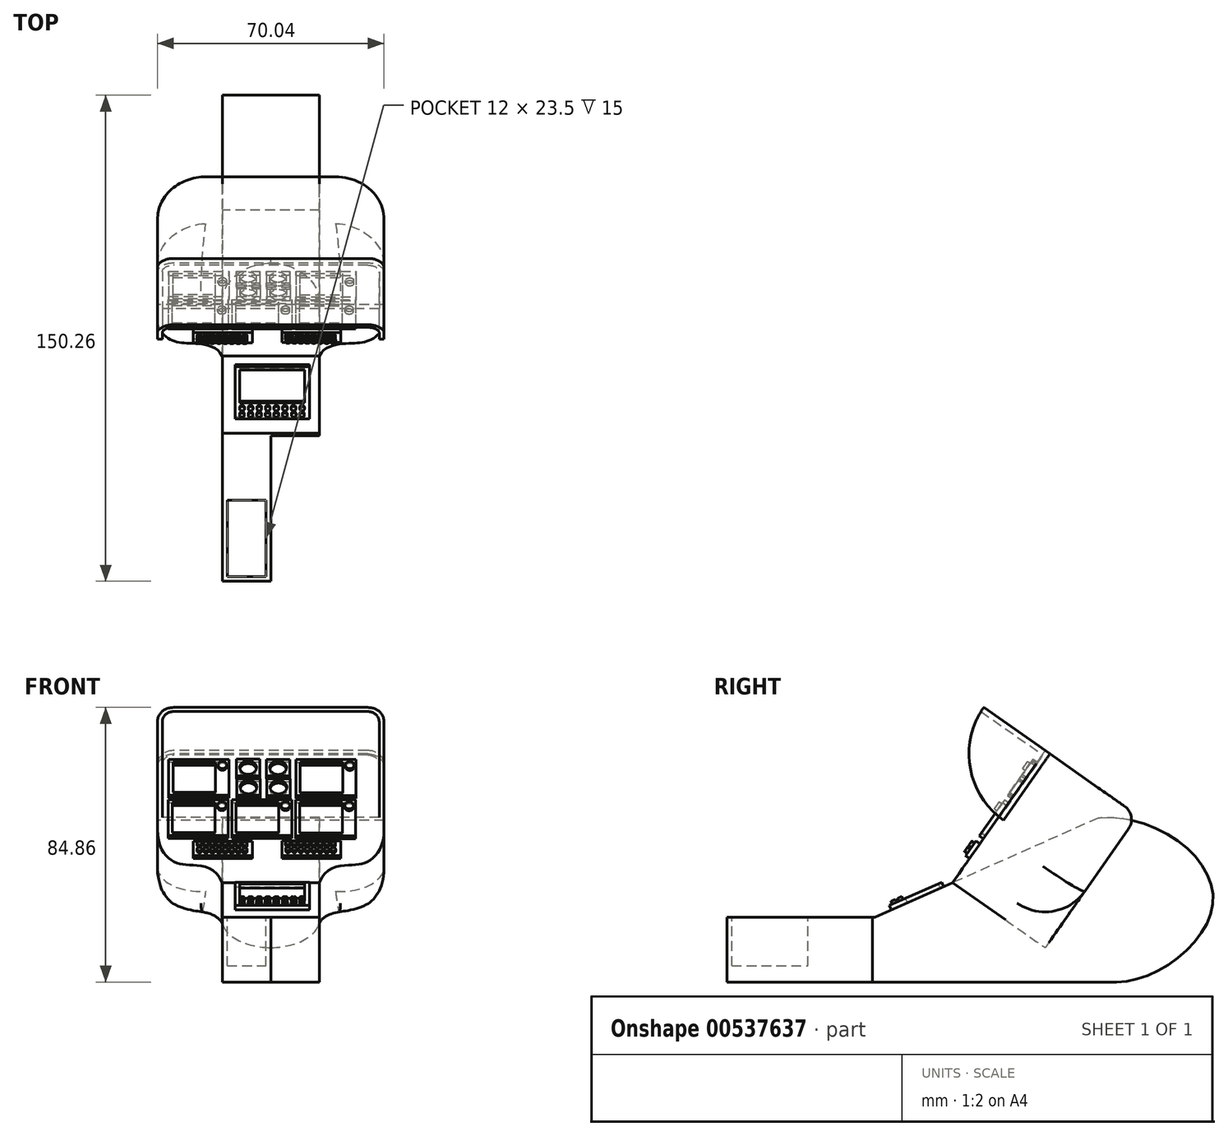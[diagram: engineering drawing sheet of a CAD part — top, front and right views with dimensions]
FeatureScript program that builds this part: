
annotation { "Feature Type Name" : "Feature", "Feature Type Description" : "" }
export const myFeature = defineFeature(function(context is Context, id is Id, definition is map)
    precondition{}
    {
        {
            var Q0;
            Q0=qCreatedBy(makeId("Right.planeOp"),FACE);
            var sketch = newSketch(context, id + "F0", { "sketchPlane" : qUnion([Q0])});
            skLineSegment(sketch, "E0", {"start": v(-60.7, 0) * mm, "end": v(59.7, 0) * mm});
            skLineSegment(sketch, "E1", {"start": v(-60.7, 0) * mm, "end": v(-60.7, 20) * mm});
            skLineSegment(sketch, "E2", {"start": v(-60.7, 20) * mm, "end": v(30.7, 20) * mm});
            skLineSegment(sketch, "E3", {"start": v(30.7, 20) * mm, "end": v(54, 50.65) * mm});
            skFitSpline(sketch, "E4", {"points": [v(59.7, 0) * mm, v(89.55, 25.37) * mm, v(54, 50.65) * mm], "startDerivative": vector(77.96, 0) * mm, "endDerivative": vector(-105.4, -8.94) * mm});
            skPoint(sketch, "E5.start.orphan", {"position": v(56.86, 25.33) * mm});
            skLineSegment(sketch, "E6", {"start": v(54, 50.65) * mm, "end": v(-15, 20) * mm});
            skSolve(sketch);
        }
        {
            var Q0;
            Q0 = qSketchRegion(id + "F0", true);
            extrude(context, id + "F1", {"entities" : qUnion([Q0]), "depth" : 30 * mm, "offsetDistance" : 25 * mm});
        }
        {
            var Q0;
            Q0=makeQuery(id+"F1.opExtrude","SWEPT_FACE",FACE,{"disambiguationData":[OSD([sQuery(id+"F0.wireOp",EDGE,"E2")])]});
            var sketch = newSketch(context, id + "F2", { "sketchPlane" : qUnion([Q0])});
            skLineSegment(sketch, "E7.bottom", {"start": v(30, -60.7) * mm, "end": v(15, -60.7) * mm});
            skLineSegment(sketch, "E7.top", {"start": v(30, -15.7) * mm, "end": v(15, -15.7) * mm});
            skLineSegment(sketch, "E7.left", {"start": v(30, -60.7) * mm, "end": v(30, -15.7) * mm});
            skLineSegment(sketch, "E7.right", {"start": v(15, -60.7) * mm, "end": v(15, -15.7) * mm});
            skSolve(sketch);
        }
        {
            var Q0;
            Q0=makeQuery(id+"F2.imprint","IMPRINT",FACE,{"disambiguationData":[TD([[makeQuery(id+"F2.imprint","IMPRINT",EDGE,{"derivedFrom":sQuery(id+"F2.wireOp",EDGE,"E7.bottom")}),-1.0]])]});
            extrude(context, id + "F3", {"entities" : qUnion([Q0]), "operationType" : NewBodyOperationType.REMOVE, "oppositeDirection" : true, "depth" : 25 * mm, "offsetDistance" : 25 * mm});
        }
        {
            var Q0;
            Q0=qCreatedBy(makeId("Front.planeOp"),FACE);
            var sketch = newSketch(context, id + "F4", { "sketchPlane" : qUnion([Q0])});
            skLineSegment(sketch, "E8.bottom", {"start": v(-58.83, 0) * mm, "end": v(-73.91, 0) * mm});
            skLineSegment(sketch, "E8.top", {"start": v(-58.83, 49.9) * mm, "end": v(-93.85, 49.9) * mm});
            skLineSegment(sketch, "E8.left", {"start": v(-58.83, 0) * mm, "end": v(-58.83, 49.9) * mm});
            skLineSegment(sketch, "E8.right", {"start": v(-93.85, 20.22) * mm, "end": v(-93.85, 49.9) * mm});
            skFitSpline(sketch, "E9", {"points": [v(-93.85, 20.22) * mm, v(-88.82, 8.01) * mm, v(-83.08, 6.66) * mm, v(-73.91, 0) * mm], "startDerivative": vector(0, -55.1) * mm, "endDerivative": vector(14.58, -51.04) * mm});
            skLineSegment(sketch, "E10.MirrorCS", {"start": v(-58.83, 0) * mm, "end": v(-43.76, 0) * mm});
            skLineSegment(sketch, "E11.MirrorCS", {"start": v(-23.81, 20.22) * mm, "end": v(-23.81, 49.9) * mm});
            skLineSegment(sketch, "E12.MirrorCS", {"start": v(-58.83, 49.9) * mm, "end": v(-23.81, 49.9) * mm});
            skFitSpline(sketch, "E13.MirrorCS", {"points": [v(-23.81, 20.22) * mm, v(-28.84, 8.01) * mm, v(-34.59, 6.66) * mm, v(-43.76, 0) * mm], "startDerivative": vector(0, -55.1) * mm, "endDerivative": vector(-14.58, -51.04) * mm});
            skSolve(sketch);
        }
        {
            var Q0;
            Q0 = qSketchRegion(id + "F4", true);
            extrude(context, id + "F5", {"entities" : qUnion([Q0]), "oppositeDirection" : true, "depth" : 35 * mm, "offsetDistance" : 25 * mm});
        }
        {
            var Q0;
            Q0=makeQuery(id+"F5.opExtrude","CAP_EDGE",EDGE,{"disambiguationData":[OSD([sQuery(id+"F4.wireOp",EDGE,"E13.MirrorCS")])],"isStart":false});
            var Q1;
            Q1=makeQuery(id+"F5.opExtrude","CAP_EDGE",EDGE,{"disambiguationData":[OSD([sQuery(id+"F4.wireOp",EDGE,"E11.MirrorCS")])],"isStart":false});
            var Q2;
            Q2=makeQuery(id+"F5.opExtrude","CAP_EDGE",EDGE,{"disambiguationData":[OSD([sQuery(id+"F4.wireOp",EDGE,"E8.right")])],"isStart":false});
            var Q3;
            Q3=makeQuery(id+"F5.opExtrude","CAP_EDGE",EDGE,{"disambiguationData":[OSD([sQuery(id+"F4.wireOp",EDGE,"E9")])],"isStart":false});
            fillet(context, id + "F6", {"entities" : qUnion([Q0, Q1, Q2, Q3]), "radius" : 15 * mm, "tangentPropagation" : true, "allowEdgeOverflow" : false});
        }
        {
            var Q0;
            Q0=makeQuery(id+"F6.opFillet","BLEND_EDGE",EDGE,{"blendedFrom":[makeQuery(id+"F5.opExtrude","CAP_EDGE",EDGE,{"disambiguationData":[OSD([sQuery(id+"F4.wireOp",EDGE,"E11.MirrorCS")])],"isStart":false}),makeQuery(id+"F5.opExtrude","SWEPT_FACE",FACE,{"disambiguationData":[OSD([sQuery(id+"F4.wireOp",EDGE,"E8.top"),sQuery(id+"F4.wireOp",EDGE,"E12.MirrorCS")])]})],"blendedInto":[makeQuery(id+"F5.opExtrude","SWEPT_FACE",FACE,{"disambiguationData":[OSD([sQuery(id+"F4.wireOp",EDGE,"E8.top"),sQuery(id+"F4.wireOp",EDGE,"E12.MirrorCS")])]})]});
            var Q1;
            Q1=makeQuery(id+"F5.opExtrude","CAP_EDGE",EDGE,{"disambiguationData":[OSD([sQuery(id+"F4.wireOp",EDGE,"E8.top"),sQuery(id+"F4.wireOp",EDGE,"E12.MirrorCS")])],"isStart":false});
            var Q2;
            Q2=makeQuery(id+"F6.opFillet","BLEND_EDGE",EDGE,{"blendedFrom":[makeQuery(id+"F5.opExtrude","CAP_EDGE",EDGE,{"disambiguationData":[OSD([sQuery(id+"F4.wireOp",EDGE,"E8.right")])],"isStart":false}),makeQuery(id+"F5.opExtrude","SWEPT_FACE",FACE,{"disambiguationData":[OSD([sQuery(id+"F4.wireOp",EDGE,"E8.top"),sQuery(id+"F4.wireOp",EDGE,"E12.MirrorCS")])]})],"blendedInto":[makeQuery(id+"F5.opExtrude","SWEPT_FACE",FACE,{"disambiguationData":[OSD([sQuery(id+"F4.wireOp",EDGE,"E8.top"),sQuery(id+"F4.wireOp",EDGE,"E12.MirrorCS")])]})]});
            fillet(context, id + "F7", {"entities" : qUnion([Q0, Q1, Q2]), "radius" : 5 * mm, "tangentPropagation" : true, "allowEdgeOverflow" : false});
        }
        {
            var Q0;
            Q0=makeQuery(id+"F5.opExtrude","SWEPT_FACE",FACE,{"disambiguationData":[OSD([sQuery(id+"F4.wireOp",EDGE,"E8.right")])]});
            var sketch = newSketch(context, id + "F8", { "sketchPlane" : qUnion([Q0])});
            skPoint(sketch, "E14.0", {"position": v(0, 49.9) * mm});
            skLineSegment(sketch, "E15", {"start": v(0, 49.9) * mm, "end": v(0, 24.9) * mm});
            skArc(sketch, "E16", {"start": v(0, 24.9) * mm, "mid": v(17.68, 32.23) * mm, "end": v(25, 49.9) * mm});
            skLineSegment(sketch, "E17", {"start": v(25, 49.9) * mm, "end": v(0, 49.9) * mm});
            skSolve(sketch);
        }
        {
            var Q0;
            {var subQ4=sQuery(id+"F8.wireOp",EDGE,"E16");Q0=makeQuery(id+"F8.imprint","IMPRINT",FACE,{"disambiguationData":[TD([[makeQuery(id+"F8.imprint","IMPRINT",EDGE,{"derivedFrom":subQ4}),1.0]])]});}
            var Q1;
            Q1=makeQuery(id+"F5.opExtrude","SWEPT_FACE",FACE,{"disambiguationData":[OSD([sQuery(id+"F4.wireOp",EDGE,"E11.MirrorCS")])]});
            extrude(context, id + "F9", {"entities" : qUnion([Q0]), "endBound" : BoundingType.UP_TO_SURFACE, "oppositeDirection" : true, "depth" : 25 * mm, "endBoundEntityFace" : qUnion([Q1]), "offsetDistance" : 25 * mm});
        }
        {
            var Q0;
            Q0=makeQuery(id+"F9.opExtrude","CAP_EDGE",EDGE,{"disambiguationData":[OSD([sQuery(id+"F8.wireOp",EDGE,"E17")])],"isStart":true});
            var Q1;
            Q1=makeQuery(id+"F9.opExtrude","CAP_EDGE",EDGE,{"disambiguationData":[OSD([sQuery(id+"F8.wireOp",EDGE,"E17")])],"isStart":false});
            fillet(context, id + "F10", {"entities" : qUnion([Q0, Q1]), "radius" : 5 * mm, "tangentPropagation" : true, "allowEdgeOverflow" : false});
        }
        {
            var Q0;
            Q0=makeQuery(id+"F9.opExtrude","SWEPT_FACE",FACE,{"disambiguationData":[OSD([sQuery(id+"F8.wireOp",EDGE,"E16")])]});
            shell(context, id + "F11", {"entities" : qUnion([Q0]), "thickness" : 1.5 * mm});
        }
        {
            var Q0;
            Q0=makeQuery(id+"F5.opExtrude","SWEPT_BODY",BODY,{"disambiguationData":[OSD([sQuery(id+"F4.wireOp",EDGE,"E8.top"),sQuery(id+"F4.wireOp",EDGE,"E8.right"),sQuery(id+"F4.wireOp",EDGE,"E8.bottom"),sQuery(id+"F4.wireOp",EDGE,"E9"),sQuery(id+"F4.wireOp",EDGE,"E11.MirrorCS"),sQuery(id+"F4.wireOp",EDGE,"E10.MirrorCS"),sQuery(id+"F4.wireOp",EDGE,"E12.MirrorCS"),sQuery(id+"F4.wireOp",EDGE,"E13.MirrorCS")])]});
            var Q1;
            Q1=makeQuery(id+"F9.opExtrude","SWEPT_BODY",BODY,{"disambiguationData":[OSD([sQuery(id+"F8.wireOp",EDGE,"E15"),sQuery(id+"F8.wireOp",EDGE,"E16"),sQuery(id+"F8.wireOp",EDGE,"E17")])]});
            var Q2;
            Q2=makeQuery(id+"F5.opExtrude","CAP_EDGE",EDGE,{"disambiguationData":[OSD([sQuery(id+"F4.wireOp",EDGE,"E8.bottom"),sQuery(id+"F4.wireOp",EDGE,"E10.MirrorCS")])],"isStart":true});
            transform(context, id + "F12", {"entities" : qUnion([Q0, Q1]), "transformType" : TransformType.ROTATION, "transformAxis" : qUnion([Q2]), "angle" : 35 * degree, "makeCopy" : false});
        }
        {
            var Q0;
            Q0=makeQuery(id+"F1.opExtrude","CAP_FACE",FACE,{"disambiguationData":[OSD([sQuery(id+"F0.wireOp",EDGE,"E0"),sQuery(id+"F0.wireOp",EDGE,"E1"),sQuery(id+"F0.wireOp",EDGE,"E2"),sQuery(id+"F0.wireOp",EDGE,"E4"),sQuery(id+"F0.wireOp",EDGE,"E6")])],"isStart":false});
            var sketch = newSketch(context, id + "F13", { "sketchPlane" : qUnion([Q0])});
            skPoint(sketch, "E18.0", {"position": v(-60.7, 0) * mm});
            skPoint(sketch, "E19", {"position": v(9, 30.67) * mm});
            skSolve(sketch);
        }
        {
            var Q0;
            Q0=makeQuery(id+"F9.opExtrude","SWEPT_BODY",BODY,{"disambiguationData":[OSD([sQuery(id+"F8.wireOp",EDGE,"E15"),sQuery(id+"F8.wireOp",EDGE,"E16"),sQuery(id+"F8.wireOp",EDGE,"E17")])]});
            var Q1;
            Q1=makeQuery(id+"F5.opExtrude","SWEPT_BODY",BODY,{"disambiguationData":[OSD([sQuery(id+"F4.wireOp",EDGE,"E8.top"),sQuery(id+"F4.wireOp",EDGE,"E8.right"),sQuery(id+"F4.wireOp",EDGE,"E8.bottom"),sQuery(id+"F4.wireOp",EDGE,"E9"),sQuery(id+"F4.wireOp",EDGE,"E11.MirrorCS"),sQuery(id+"F4.wireOp",EDGE,"E10.MirrorCS"),sQuery(id+"F4.wireOp",EDGE,"E12.MirrorCS"),sQuery(id+"F4.wireOp",EDGE,"E13.MirrorCS")])]});
            var Q2;
            Q2=makeQuery(id+"F5.opExtrude","CAP_VERTEX",VERTEX,{"disambiguationData":[OSD([sQuery(id+"F4.wireOp",EDGE,"E10.MirrorCS"),sQuery(id+"F4.wireOp",EDGE,"E13.MirrorCS")])],"isStart":true});
            var Q3;
            Q3=sQuery(id+"F13.wireOp",VERTEX,"E19");
            transform(context, id + "F14", {"entities" : qUnion([Q0, Q1]), "transformType" : TransformType.TRANSLATION_ENTITY, "oppositeDirectionEntity" : false, "transformLine" : qUnion([Q2, Q3]), "makeCopy" : false});
        }
        {
            var Q0;
            Q0=makeQuery(id+"F9.opExtrude","CAP_FACE",FACE,{"disambiguationData":[OSD([sQuery(id+"F8.wireOp",EDGE,"E15"),sQuery(id+"F8.wireOp",EDGE,"E16"),sQuery(id+"F8.wireOp",EDGE,"E17")])],"isStart":false});
            var sketch = newSketch(context, id + "F15", { "sketchPlane" : qUnion([Q0])});
            skLineSegment(sketch, "E20", {"start": v(29.02, 59.26) * mm, "end": v(30.5, 58.23) * mm});
            skSolve(sketch);
        }
        {
            var Q0;
            Q0=makeQuery(id+"F9.opExtrude","SWEPT_BODY",BODY,{"disambiguationData":[OSD([sQuery(id+"F8.wireOp",EDGE,"E15"),sQuery(id+"F8.wireOp",EDGE,"E16"),sQuery(id+"F8.wireOp",EDGE,"E17")])]});
            var Q1;
            Q1=sQuery(id+"F15.wireOp",VERTEX,"E20.start");
            var Q2;
            Q2=sQuery(id+"F15.wireOp",VERTEX,"E20.end");
            transform(context, id + "F16", {"entities" : qUnion([Q0]), "transformType" : TransformType.TRANSLATION_ENTITY, "oppositeDirectionEntity" : false, "transformLine" : qUnion([Q1, Q2]), "makeCopy" : false});
        }
        {
            var Q0;
            Q0=makeQuery(id+"F1.opExtrude","SWEPT_FACE",FACE,{"disambiguationData":[OSD([sQuery(id+"F0.wireOp",EDGE,"E2")])]});
            var sketch = newSketch(context, id + "F17", { "sketchPlane" : qUnion([Q0])});
            skLineSegment(sketch, "E21", {"start": v(0, -60.7) * mm, "end": v(1.5, -60.7) * mm});
            skLineSegment(sketch, "E22", {"start": v(1.5, -60.7) * mm, "end": v(1.5, -59.2) * mm});
            skLineSegment(sketch, "E23.bottom", {"start": v(1.5, -59.2) * mm, "end": v(13.5, -59.2) * mm});
            skLineSegment(sketch, "E23.top", {"start": v(1.5, -35.7) * mm, "end": v(13.5, -35.7) * mm});
            skLineSegment(sketch, "E23.left", {"start": v(1.5, -59.2) * mm, "end": v(1.5, -35.7) * mm});
            skLineSegment(sketch, "E23.right", {"start": v(13.5, -59.2) * mm, "end": v(13.5, -35.7) * mm});
            skSolve(sketch);
        }
        {
            var Q0;
            Q0=makeQuery(id+"F17.imprint","IMPRINT",FACE,{"disambiguationData":[TD([[makeQuery(id+"F17.imprint","IMPRINT",EDGE,{"derivedFrom":sQuery(id+"F17.wireOp",EDGE,"E23.bottom")}),1.0]])]});
            extrude(context, id + "F18", {"entities" : qUnion([Q0]), "operationType" : NewBodyOperationType.REMOVE, "oppositeDirection" : true, "depth" : 15 * mm, "offsetDistance" : 25 * mm});
        }
        {
            var Q0;
            Q0=makeQuery(id+"F5.opExtrude","CAP_FACE",FACE,{"disambiguationData":[OSD([sQuery(id+"F4.wireOp",EDGE,"E8.top"),sQuery(id+"F4.wireOp",EDGE,"E8.right"),sQuery(id+"F4.wireOp",EDGE,"E8.bottom"),sQuery(id+"F4.wireOp",EDGE,"E9"),sQuery(id+"F4.wireOp",EDGE,"E11.MirrorCS"),sQuery(id+"F4.wireOp",EDGE,"E10.MirrorCS"),sQuery(id+"F4.wireOp",EDGE,"E12.MirrorCS"),sQuery(id+"F4.wireOp",EDGE,"E13.MirrorCS")])],"isStart":true});
            var sketch = newSketch(context, id + "F19", { "sketchPlane" : qUnion([Q0])});
            skLineSegment(sketch, "E24.bottom", {"start": v(-16.58, 75.82) * mm, "end": v(1.98, 75.82) * mm});
            skLineSegment(sketch, "E24.top", {"start": v(-16.58, 62.23) * mm, "end": v(1.98, 62.23) * mm});
            skLineSegment(sketch, "E24.left", {"start": v(-16.58, 75.82) * mm, "end": v(-16.58, 62.23) * mm});
            skLineSegment(sketch, "E24.right", {"start": v(1.98, 75.82) * mm, "end": v(1.98, 62.23) * mm});
            skPoint(sketch, "E25.oppositeSnap0", {"position": v(-20.1, 62.85) * mm});
            skLineSegment(sketch, "E26.bottom", {"start": v(-15.3, 63.3) * mm, "end": v(-2.13, 63.3) * mm});
            skLineSegment(sketch, "E26.top", {"start": v(-15.3, 74.71) * mm, "end": v(-2.13, 74.71) * mm});
            skLineSegment(sketch, "E26.left", {"start": v(-15.3, 63.3) * mm, "end": v(-15.3, 74.71) * mm});
            skLineSegment(sketch, "E26.right", {"start": v(-2.13, 63.3) * mm, "end": v(-2.13, 74.71) * mm});
            skCircle(sketch, "E27", {"center": v(0, 73.02) * mm, "radius": 1.34 * mm});
            skLineSegment(sketch, "E28.bottom", {"start": v(22.78, 75.76) * mm, "end": v(41.33, 75.76) * mm});
            skLineSegment(sketch, "E28.top", {"start": v(22.78, 62.16) * mm, "end": v(41.33, 62.16) * mm});
            skLineSegment(sketch, "E28.left", {"start": v(22.78, 75.76) * mm, "end": v(22.78, 62.16) * mm});
            skLineSegment(sketch, "E28.right", {"start": v(41.33, 75.76) * mm, "end": v(41.33, 62.16) * mm});
            skLineSegment(sketch, "E29.bottom", {"start": v(24.05, 63.25) * mm, "end": v(37.23, 63.25) * mm});
            skLineSegment(sketch, "E29.top", {"start": v(24.05, 74.65) * mm, "end": v(37.23, 74.65) * mm});
            skLineSegment(sketch, "E29.left", {"start": v(24.05, 63.25) * mm, "end": v(24.05, 74.65) * mm});
            skLineSegment(sketch, "E29.right", {"start": v(37.23, 63.25) * mm, "end": v(37.23, 74.65) * mm});
            skCircle(sketch, "E30", {"center": v(39.36, 72.96) * mm, "radius": 1.34 * mm});
            skLineSegment(sketch, "E31.bottom", {"start": v(-16.76, 60.6) * mm, "end": v(1.8, 60.6) * mm});
            skLineSegment(sketch, "E31.top", {"start": v(-16.76, 47.01) * mm, "end": v(1.8, 47.01) * mm});
            skLineSegment(sketch, "E31.left", {"start": v(-16.76, 60.6) * mm, "end": v(-16.76, 47.01) * mm});
            skLineSegment(sketch, "E31.right", {"start": v(1.8, 60.6) * mm, "end": v(1.8, 47.01) * mm});
            skLineSegment(sketch, "E32.bottom", {"start": v(-15.48, 48.1) * mm, "end": v(-2.3, 48.1) * mm});
            skLineSegment(sketch, "E32.top", {"start": v(-15.48, 59.5) * mm, "end": v(-2.3, 59.5) * mm});
            skLineSegment(sketch, "E32.left", {"start": v(-15.48, 48.1) * mm, "end": v(-15.48, 59.5) * mm});
            skLineSegment(sketch, "E32.right", {"start": v(-2.3, 48.1) * mm, "end": v(-2.3, 59.5) * mm});
            skCircle(sketch, "E33", {"center": v(-0.17, 57.8) * mm, "radius": 1.34 * mm});
            skLineSegment(sketch, "E34.bottom", {"start": v(22.6, 60.54) * mm, "end": v(41.16, 60.54) * mm});
            skLineSegment(sketch, "E34.top", {"start": v(22.6, 46.95) * mm, "end": v(41.16, 46.95) * mm});
            skLineSegment(sketch, "E34.left", {"start": v(22.6, 60.54) * mm, "end": v(22.6, 46.95) * mm});
            skLineSegment(sketch, "E34.right", {"start": v(41.16, 60.54) * mm, "end": v(41.16, 46.95) * mm});
            skLineSegment(sketch, "E35.bottom", {"start": v(23.87, 48.04) * mm, "end": v(37.05, 48.04) * mm});
            skLineSegment(sketch, "E35.top", {"start": v(23.87, 59.44) * mm, "end": v(37.05, 59.44) * mm});
            skLineSegment(sketch, "E35.left", {"start": v(23.87, 48.04) * mm, "end": v(23.87, 59.44) * mm});
            skLineSegment(sketch, "E35.right", {"start": v(37.05, 48.04) * mm, "end": v(37.05, 59.44) * mm});
            skCircle(sketch, "E36", {"center": v(39.18, 57.74) * mm, "radius": 1.34 * mm});
            skLineSegment(sketch, "E37.bottom", {"start": v(2.9, 60.6) * mm, "end": v(21.46, 60.6) * mm});
            skLineSegment(sketch, "E37.top", {"start": v(2.9, 47.01) * mm, "end": v(21.46, 47.01) * mm});
            skLineSegment(sketch, "E37.left", {"start": v(2.9, 60.6) * mm, "end": v(2.9, 47.01) * mm});
            skLineSegment(sketch, "E37.right", {"start": v(21.46, 60.6) * mm, "end": v(21.46, 47.01) * mm});
            skLineSegment(sketch, "E38.bottom", {"start": v(4.17, 48.1) * mm, "end": v(17.35, 48.1) * mm});
            skLineSegment(sketch, "E38.top", {"start": v(4.17, 59.5) * mm, "end": v(17.35, 59.5) * mm});
            skLineSegment(sketch, "E38.left", {"start": v(4.17, 48.1) * mm, "end": v(4.17, 59.5) * mm});
            skLineSegment(sketch, "E38.right", {"start": v(17.35, 48.1) * mm, "end": v(17.35, 59.5) * mm});
            skCircle(sketch, "E39", {"center": v(19.48, 57.8) * mm, "radius": 1.34 * mm});
            skLineSegment(sketch, "E40.bottom", {"start": v(4.34, 75.87) * mm, "end": v(11.54, 75.87) * mm});
            skLineSegment(sketch, "E40.top", {"start": v(4.34, 69.53) * mm, "end": v(11.54, 69.53) * mm});
            skLineSegment(sketch, "E40.left", {"start": v(4.34, 75.87) * mm, "end": v(4.34, 69.53) * mm});
            skLineSegment(sketch, "E40.right", {"start": v(11.54, 75.87) * mm, "end": v(11.54, 69.53) * mm});
            skCircle(sketch, "E41", {"center": v(7.94, 72.7) * mm, "radius": 2.58 * mm});
            skLineSegment(sketch, "E42.1.0.0", {"start": v(13.6, 69.5) * mm, "end": v(20.8, 69.5) * mm});
            skCircle(sketch, "E42.1.0.1", {"center": v(17.2, 72.67) * mm, "radius": 2.58 * mm});
            skLineSegment(sketch, "E42.1.0.2", {"start": v(20.8, 75.84) * mm, "end": v(20.8, 69.5) * mm});
            skLineSegment(sketch, "E42.1.0.3", {"start": v(13.6, 75.84) * mm, "end": v(13.6, 69.5) * mm});
            skLineSegment(sketch, "E42.1.0.4", {"start": v(13.6, 75.84) * mm, "end": v(20.8, 75.84) * mm});
            skLineSegment(sketch, "E42.direction1", {"start": v(4.34, 69.53) * mm, "end": v(13.6, 69.5) * mm, "construction": true});
            skLineSegment(sketch, "E43.bottom", {"start": v(4.45, 68.55) * mm, "end": v(11.65, 68.55) * mm});
            skLineSegment(sketch, "E43.top", {"start": v(4.45, 62.2) * mm, "end": v(11.65, 62.2) * mm});
            skLineSegment(sketch, "E43.left", {"start": v(4.45, 68.55) * mm, "end": v(4.45, 62.2) * mm});
            skLineSegment(sketch, "E43.right", {"start": v(11.65, 68.55) * mm, "end": v(11.65, 62.2) * mm});
            skCircle(sketch, "E44", {"center": v(8.05, 65.38) * mm, "radius": 2.58 * mm});
            skLineSegment(sketch, "E45.1.0.0", {"start": v(13.72, 62.18) * mm, "end": v(20.92, 62.18) * mm});
            skCircle(sketch, "E45.1.0.1", {"center": v(17.32, 65.35) * mm, "radius": 2.58 * mm});
            skLineSegment(sketch, "E45.1.0.2", {"start": v(20.92, 68.52) * mm, "end": v(20.92, 62.18) * mm});
            skLineSegment(sketch, "E45.1.0.3", {"start": v(13.72, 68.52) * mm, "end": v(13.72, 62.18) * mm});
            skLineSegment(sketch, "E45.1.0.4", {"start": v(13.72, 68.52) * mm, "end": v(20.92, 68.52) * mm});
            skLineSegment(sketch, "E45.direction1", {"start": v(4.45, 62.2) * mm, "end": v(13.72, 62.18) * mm, "construction": true});
            skLineSegment(sketch, "E46.bottom", {"start": v(-8.98, 44.92) * mm, "end": v(9.3, 44.92) * mm});
            skLineSegment(sketch, "E46.top", {"start": v(-8.98, 39.41) * mm, "end": v(9.3, 39.41) * mm});
            skLineSegment(sketch, "E46.left", {"start": v(-8.98, 44.92) * mm, "end": v(-8.98, 39.41) * mm});
            skLineSegment(sketch, "E46.right", {"start": v(9.3, 44.92) * mm, "end": v(9.3, 39.41) * mm});
            skCircle(sketch, "E47", {"center": v(-7.1, 41.24) * mm, "radius": 0.75 * mm});
            skCircle(sketch, "E48.1.0.0", {"center": v(-5.1, 41.21) * mm, "radius": 0.75 * mm});
            skCircle(sketch, "E48.2.0.0", {"center": v(-3.1, 41.18) * mm, "radius": 0.75 * mm});
            skCircle(sketch, "E48.3.0.0", {"center": v(-1.1, 41.16) * mm, "radius": 0.75 * mm});
            skCircle(sketch, "E48.4.0.0", {"center": v(0.9, 41.13) * mm, "radius": 0.75 * mm});
            skCircle(sketch, "E48.5.0.0", {"center": v(2.9, 41.1) * mm, "radius": 0.75 * mm});
            skCircle(sketch, "E48.6.0.0", {"center": v(4.9, 41.07) * mm, "radius": 0.75 * mm});
            skCircle(sketch, "E48.7.0.0", {"center": v(6.9, 41.05) * mm, "radius": 0.75 * mm});
            skLineSegment(sketch, "E48.direction1", {"start": v(-7.1, 41.24) * mm, "end": v(-5.1, 41.21) * mm, "construction": true});
            skCircle(sketch, "E49", {"center": v(-7.12, 43.45) * mm, "radius": 0.75 * mm});
            skCircle(sketch, "E50.1.0.0", {"center": v(-5.12, 43.42) * mm, "radius": 0.75 * mm});
            skCircle(sketch, "E50.2.0.0", {"center": v(-3.12, 43.4) * mm, "radius": 0.75 * mm});
            skCircle(sketch, "E50.3.0.0", {"center": v(-1.12, 43.37) * mm, "radius": 0.75 * mm});
            skCircle(sketch, "E50.4.0.0", {"center": v(0.88, 43.34) * mm, "radius": 0.75 * mm});
            skCircle(sketch, "E50.5.0.0", {"center": v(2.88, 43.31) * mm, "radius": 0.75 * mm});
            skCircle(sketch, "E50.6.0.0", {"center": v(4.88, 43.29) * mm, "radius": 0.75 * mm});
            skCircle(sketch, "E50.7.0.0", {"center": v(6.88, 43.26) * mm, "radius": 0.75 * mm});
            skLineSegment(sketch, "E50.direction1", {"start": v(-7.12, 43.45) * mm, "end": v(-5.12, 43.42) * mm, "construction": true});
            skLineSegment(sketch, "E51.bottom", {"start": v(18.36, 45.03) * mm, "end": v(36.63, 45.03) * mm});
            skLineSegment(sketch, "E51.top", {"start": v(18.36, 39.52) * mm, "end": v(36.63, 39.52) * mm});
            skLineSegment(sketch, "E51.left", {"start": v(18.36, 45.03) * mm, "end": v(18.36, 39.52) * mm});
            skLineSegment(sketch, "E51.right", {"start": v(36.63, 45.03) * mm, "end": v(36.63, 39.52) * mm});
            skCircle(sketch, "E52", {"center": v(20.25, 41.35) * mm, "radius": 0.75 * mm});
            skCircle(sketch, "E53.1.0.0", {"center": v(22.25, 41.32) * mm, "radius": 0.75 * mm});
            skCircle(sketch, "E53.2.0.0", {"center": v(24.25, 41.3) * mm, "radius": 0.75 * mm});
            skCircle(sketch, "E53.3.0.0", {"center": v(26.25, 41.27) * mm, "radius": 0.75 * mm});
            skCircle(sketch, "E53.4.0.0", {"center": v(28.25, 41.24) * mm, "radius": 0.75 * mm});
            skCircle(sketch, "E53.5.0.0", {"center": v(30.25, 41.21) * mm, "radius": 0.75 * mm});
            skCircle(sketch, "E53.6.0.0", {"center": v(32.25, 41.18) * mm, "radius": 0.75 * mm});
            skCircle(sketch, "E53.7.0.0", {"center": v(34.25, 41.16) * mm, "radius": 0.75 * mm});
            skLineSegment(sketch, "E53.direction1", {"start": v(20.25, 41.35) * mm, "end": v(22.25, 41.32) * mm, "construction": true});
            skCircle(sketch, "E54", {"center": v(20.23, 43.56) * mm, "radius": 0.75 * mm});
            skCircle(sketch, "E55.1.0.0", {"center": v(22.23, 43.53) * mm, "radius": 0.75 * mm});
            skCircle(sketch, "E55.2.0.0", {"center": v(24.23, 43.5) * mm, "radius": 0.75 * mm});
            skCircle(sketch, "E55.3.0.0", {"center": v(26.23, 43.48) * mm, "radius": 0.75 * mm});
            skCircle(sketch, "E55.4.0.0", {"center": v(28.23, 43.45) * mm, "radius": 0.75 * mm});
            skCircle(sketch, "E55.5.0.0", {"center": v(30.23, 43.42) * mm, "radius": 0.75 * mm});
            skCircle(sketch, "E55.6.0.0", {"center": v(32.23, 43.4) * mm, "radius": 0.75 * mm});
            skCircle(sketch, "E55.7.0.0", {"center": v(34.23, 43.37) * mm, "radius": 0.75 * mm});
            skLineSegment(sketch, "E55.direction1", {"start": v(20.23, 43.56) * mm, "end": v(22.23, 43.53) * mm, "construction": true});
            skSolve(sketch);
        }
        {
            var Q0;
            Q0=makeQuery(id+"F19.imprint","IMPRINT",FACE,{"disambiguationData":[TD([[makeQuery(id+"F19.imprint","IMPRINT",EDGE,{"derivedFrom":sQuery(id+"F19.wireOp",EDGE,"E24.bottom")}),-1.0]])]});
            var Q1;
            Q1=makeQuery(id+"F19.imprint","IMPRINT",FACE,{"disambiguationData":[TD([[makeQuery(id+"F19.imprint","IMPRINT",EDGE,{"derivedFrom":sQuery(id+"F19.wireOp",EDGE,"E31.bottom")}),-1.0]])]});
            var Q2;
            Q2=makeQuery(id+"F19.imprint","IMPRINT",FACE,{"disambiguationData":[TD([[makeQuery(id+"F19.imprint","IMPRINT",EDGE,{"derivedFrom":sQuery(id+"F19.wireOp",EDGE,"E37.bottom")}),-1.0]])]});
            var Q3;
            Q3=makeQuery(id+"F19.imprint","IMPRINT",FACE,{"disambiguationData":[TD([[makeQuery(id+"F19.imprint","IMPRINT",EDGE,{"derivedFrom":sQuery(id+"F19.wireOp",EDGE,"E34.bottom")}),-1.0]])]});
            var Q4;
            Q4=makeQuery(id+"F19.imprint","IMPRINT",FACE,{"disambiguationData":[TD([[makeQuery(id+"F19.imprint","IMPRINT",EDGE,{"derivedFrom":sQuery(id+"F19.wireOp",EDGE,"E28.bottom")}),-1.0]])]});
            var Q5;
            Q5=makeQuery(id+"F19.imprint","IMPRINT",FACE,{"disambiguationData":[TD([[makeQuery(id+"F19.imprint","IMPRINT",EDGE,{"derivedFrom":sQuery(id+"F19.wireOp",EDGE,"E45.1.0.0")}),1.0]])]});
            var Q6;
            Q6=makeQuery(id+"F19.imprint","IMPRINT",FACE,{"disambiguationData":[TD([[makeQuery(id+"F19.imprint","IMPRINT",EDGE,{"derivedFrom":sQuery(id+"F19.wireOp",EDGE,"E43.bottom")}),-1.0]])]});
            var Q7;
            Q7=makeQuery(id+"F19.imprint","IMPRINT",FACE,{"disambiguationData":[TD([[makeQuery(id+"F19.imprint","IMPRINT",EDGE,{"derivedFrom":sQuery(id+"F19.wireOp",EDGE,"E40.bottom")}),-1.0]])]});
            var Q8;
            Q8=makeQuery(id+"F19.imprint","IMPRINT",FACE,{"disambiguationData":[TD([[makeQuery(id+"F19.imprint","IMPRINT",EDGE,{"derivedFrom":sQuery(id+"F19.wireOp",EDGE,"E42.1.0.0")}),1.0]])]});
            var Q9;
            Q9=makeQuery(id+"F19.imprint","IMPRINT",FACE,{"disambiguationData":[TD([[makeQuery(id+"F19.imprint","IMPRINT",EDGE,{"derivedFrom":sQuery(id+"F19.wireOp",EDGE,"E46.bottom")}),-1.0]])]});
            var Q10;
            Q10=makeQuery(id+"F19.imprint","IMPRINT",FACE,{"disambiguationData":[TD([[makeQuery(id+"F19.imprint","IMPRINT",EDGE,{"derivedFrom":sQuery(id+"F19.wireOp",EDGE,"E51.bottom")}),-1.0]])]});
            extrude(context, id + "F20", {"entities" : qUnion([Q0, Q1, Q2, Q3, Q4, Q5, Q6, Q7, Q8, Q9, Q10]), "operationType" : NewBodyOperationType.ADD, "depth" : 1.5 * mm, "offsetDistance" : 25 * mm});
        }
        {
            var Q0;
            Q0=makeQuery(id+"F20.boolean.opBoolean","SPLIT",FACE,{"disambiguationData":[TD([makeQuery(id+"F20.opExtrude","SWEPT_FACE",FACE,{"disambiguationData":[OSD([sQuery(id+"F19.wireOp",EDGE,"E27")])]})])],"derivedFrom":makeQuery(id+"F5.opExtrude","CAP_FACE",FACE,{"disambiguationData":[OSD([sQuery(id+"F4.wireOp",EDGE,"E8.top"),sQuery(id+"F4.wireOp",EDGE,"E8.right"),sQuery(id+"F4.wireOp",EDGE,"E8.bottom"),sQuery(id+"F4.wireOp",EDGE,"E9"),sQuery(id+"F4.wireOp",EDGE,"E11.MirrorCS"),sQuery(id+"F4.wireOp",EDGE,"E10.MirrorCS"),sQuery(id+"F4.wireOp",EDGE,"E12.MirrorCS"),sQuery(id+"F4.wireOp",EDGE,"E13.MirrorCS")])],"isStart":true})});
            var Q1;
            Q1=makeQuery(id+"F20.boolean.opBoolean","SPLIT",FACE,{"disambiguationData":[TD([makeQuery(id+"F20.opExtrude","SWEPT_FACE",FACE,{"disambiguationData":[OSD([sQuery(id+"F19.wireOp",EDGE,"E33")])]})])],"derivedFrom":makeQuery(id+"F5.opExtrude","CAP_FACE",FACE,{"disambiguationData":[OSD([sQuery(id+"F4.wireOp",EDGE,"E8.top"),sQuery(id+"F4.wireOp",EDGE,"E8.right"),sQuery(id+"F4.wireOp",EDGE,"E8.bottom"),sQuery(id+"F4.wireOp",EDGE,"E9"),sQuery(id+"F4.wireOp",EDGE,"E11.MirrorCS"),sQuery(id+"F4.wireOp",EDGE,"E10.MirrorCS"),sQuery(id+"F4.wireOp",EDGE,"E12.MirrorCS"),sQuery(id+"F4.wireOp",EDGE,"E13.MirrorCS")])],"isStart":true})});
            var Q2;
            Q2=makeQuery(id+"F20.boolean.opBoolean","SPLIT",FACE,{"disambiguationData":[TD([makeQuery(id+"F20.opExtrude","SWEPT_FACE",FACE,{"disambiguationData":[OSD([sQuery(id+"F19.wireOp",EDGE,"E39")])]})])],"derivedFrom":makeQuery(id+"F5.opExtrude","CAP_FACE",FACE,{"disambiguationData":[OSD([sQuery(id+"F4.wireOp",EDGE,"E8.top"),sQuery(id+"F4.wireOp",EDGE,"E8.right"),sQuery(id+"F4.wireOp",EDGE,"E8.bottom"),sQuery(id+"F4.wireOp",EDGE,"E9"),sQuery(id+"F4.wireOp",EDGE,"E11.MirrorCS"),sQuery(id+"F4.wireOp",EDGE,"E10.MirrorCS"),sQuery(id+"F4.wireOp",EDGE,"E12.MirrorCS"),sQuery(id+"F4.wireOp",EDGE,"E13.MirrorCS")])],"isStart":true})});
            var Q3;
            Q3=makeQuery(id+"F20.boolean.opBoolean","SPLIT",FACE,{"disambiguationData":[TD([makeQuery(id+"F20.opExtrude","SWEPT_FACE",FACE,{"disambiguationData":[OSD([sQuery(id+"F19.wireOp",EDGE,"E36")])]})])],"derivedFrom":makeQuery(id+"F5.opExtrude","CAP_FACE",FACE,{"disambiguationData":[OSD([sQuery(id+"F4.wireOp",EDGE,"E8.top"),sQuery(id+"F4.wireOp",EDGE,"E8.right"),sQuery(id+"F4.wireOp",EDGE,"E8.bottom"),sQuery(id+"F4.wireOp",EDGE,"E9"),sQuery(id+"F4.wireOp",EDGE,"E11.MirrorCS"),sQuery(id+"F4.wireOp",EDGE,"E10.MirrorCS"),sQuery(id+"F4.wireOp",EDGE,"E12.MirrorCS"),sQuery(id+"F4.wireOp",EDGE,"E13.MirrorCS")])],"isStart":true})});
            var Q4;
            Q4=makeQuery(id+"F20.boolean.opBoolean","SPLIT",FACE,{"disambiguationData":[TD([makeQuery(id+"F20.opExtrude","SWEPT_FACE",FACE,{"disambiguationData":[OSD([sQuery(id+"F19.wireOp",EDGE,"E30")])]})])],"derivedFrom":makeQuery(id+"F5.opExtrude","CAP_FACE",FACE,{"disambiguationData":[OSD([sQuery(id+"F4.wireOp",EDGE,"E8.top"),sQuery(id+"F4.wireOp",EDGE,"E8.right"),sQuery(id+"F4.wireOp",EDGE,"E8.bottom"),sQuery(id+"F4.wireOp",EDGE,"E9"),sQuery(id+"F4.wireOp",EDGE,"E11.MirrorCS"),sQuery(id+"F4.wireOp",EDGE,"E10.MirrorCS"),sQuery(id+"F4.wireOp",EDGE,"E12.MirrorCS"),sQuery(id+"F4.wireOp",EDGE,"E13.MirrorCS")])],"isStart":true})});
            var Q5;
            Q5=makeQuery(id+"F20.boolean.opBoolean","SPLIT",FACE,{"disambiguationData":[TD([makeQuery(id+"F20.opExtrude","SWEPT_FACE",FACE,{"disambiguationData":[OSD([sQuery(id+"F19.wireOp",EDGE,"E49")])]})])],"derivedFrom":makeQuery(id+"F5.opExtrude","CAP_FACE",FACE,{"disambiguationData":[OSD([sQuery(id+"F4.wireOp",EDGE,"E8.top"),sQuery(id+"F4.wireOp",EDGE,"E8.right"),sQuery(id+"F4.wireOp",EDGE,"E8.bottom"),sQuery(id+"F4.wireOp",EDGE,"E9"),sQuery(id+"F4.wireOp",EDGE,"E11.MirrorCS"),sQuery(id+"F4.wireOp",EDGE,"E10.MirrorCS"),sQuery(id+"F4.wireOp",EDGE,"E12.MirrorCS"),sQuery(id+"F4.wireOp",EDGE,"E13.MirrorCS")])],"isStart":true})});
            var Q6;
            Q6=makeQuery(id+"F20.boolean.opBoolean","SPLIT",FACE,{"disambiguationData":[TD([makeQuery(id+"F20.opExtrude","SWEPT_FACE",FACE,{"disambiguationData":[OSD([sQuery(id+"F19.wireOp",EDGE,"E50.1.0.0")])]})])],"derivedFrom":makeQuery(id+"F5.opExtrude","CAP_FACE",FACE,{"disambiguationData":[OSD([sQuery(id+"F4.wireOp",EDGE,"E8.top"),sQuery(id+"F4.wireOp",EDGE,"E8.right"),sQuery(id+"F4.wireOp",EDGE,"E8.bottom"),sQuery(id+"F4.wireOp",EDGE,"E9"),sQuery(id+"F4.wireOp",EDGE,"E11.MirrorCS"),sQuery(id+"F4.wireOp",EDGE,"E10.MirrorCS"),sQuery(id+"F4.wireOp",EDGE,"E12.MirrorCS"),sQuery(id+"F4.wireOp",EDGE,"E13.MirrorCS")])],"isStart":true})});
            var Q7;
            Q7=makeQuery(id+"F20.boolean.opBoolean","SPLIT",FACE,{"disambiguationData":[TD([makeQuery(id+"F20.opExtrude","SWEPT_FACE",FACE,{"disambiguationData":[OSD([sQuery(id+"F19.wireOp",EDGE,"E50.2.0.0")])]})])],"derivedFrom":makeQuery(id+"F5.opExtrude","CAP_FACE",FACE,{"disambiguationData":[OSD([sQuery(id+"F4.wireOp",EDGE,"E8.top"),sQuery(id+"F4.wireOp",EDGE,"E8.right"),sQuery(id+"F4.wireOp",EDGE,"E8.bottom"),sQuery(id+"F4.wireOp",EDGE,"E9"),sQuery(id+"F4.wireOp",EDGE,"E11.MirrorCS"),sQuery(id+"F4.wireOp",EDGE,"E10.MirrorCS"),sQuery(id+"F4.wireOp",EDGE,"E12.MirrorCS"),sQuery(id+"F4.wireOp",EDGE,"E13.MirrorCS")])],"isStart":true})});
            var Q8;
            Q8=makeQuery(id+"F20.boolean.opBoolean","SPLIT",FACE,{"disambiguationData":[TD([makeQuery(id+"F20.opExtrude","SWEPT_FACE",FACE,{"disambiguationData":[OSD([sQuery(id+"F19.wireOp",EDGE,"E50.3.0.0")])]})])],"derivedFrom":makeQuery(id+"F5.opExtrude","CAP_FACE",FACE,{"disambiguationData":[OSD([sQuery(id+"F4.wireOp",EDGE,"E8.top"),sQuery(id+"F4.wireOp",EDGE,"E8.right"),sQuery(id+"F4.wireOp",EDGE,"E8.bottom"),sQuery(id+"F4.wireOp",EDGE,"E9"),sQuery(id+"F4.wireOp",EDGE,"E11.MirrorCS"),sQuery(id+"F4.wireOp",EDGE,"E10.MirrorCS"),sQuery(id+"F4.wireOp",EDGE,"E12.MirrorCS"),sQuery(id+"F4.wireOp",EDGE,"E13.MirrorCS")])],"isStart":true})});
            var Q9;
            Q9=makeQuery(id+"F20.boolean.opBoolean","SPLIT",FACE,{"disambiguationData":[TD([makeQuery(id+"F20.opExtrude","SWEPT_FACE",FACE,{"disambiguationData":[OSD([sQuery(id+"F19.wireOp",EDGE,"E50.4.0.0")])]})])],"derivedFrom":makeQuery(id+"F5.opExtrude","CAP_FACE",FACE,{"disambiguationData":[OSD([sQuery(id+"F4.wireOp",EDGE,"E8.top"),sQuery(id+"F4.wireOp",EDGE,"E8.right"),sQuery(id+"F4.wireOp",EDGE,"E8.bottom"),sQuery(id+"F4.wireOp",EDGE,"E9"),sQuery(id+"F4.wireOp",EDGE,"E11.MirrorCS"),sQuery(id+"F4.wireOp",EDGE,"E10.MirrorCS"),sQuery(id+"F4.wireOp",EDGE,"E12.MirrorCS"),sQuery(id+"F4.wireOp",EDGE,"E13.MirrorCS")])],"isStart":true})});
            var Q10;
            Q10=makeQuery(id+"F20.boolean.opBoolean","SPLIT",FACE,{"disambiguationData":[TD([makeQuery(id+"F20.opExtrude","SWEPT_FACE",FACE,{"disambiguationData":[OSD([sQuery(id+"F19.wireOp",EDGE,"E50.5.0.0")])]})])],"derivedFrom":makeQuery(id+"F5.opExtrude","CAP_FACE",FACE,{"disambiguationData":[OSD([sQuery(id+"F4.wireOp",EDGE,"E8.top"),sQuery(id+"F4.wireOp",EDGE,"E8.right"),sQuery(id+"F4.wireOp",EDGE,"E8.bottom"),sQuery(id+"F4.wireOp",EDGE,"E9"),sQuery(id+"F4.wireOp",EDGE,"E11.MirrorCS"),sQuery(id+"F4.wireOp",EDGE,"E10.MirrorCS"),sQuery(id+"F4.wireOp",EDGE,"E12.MirrorCS"),sQuery(id+"F4.wireOp",EDGE,"E13.MirrorCS")])],"isStart":true})});
            var Q11;
            Q11=makeQuery(id+"F20.boolean.opBoolean","SPLIT",FACE,{"disambiguationData":[TD([makeQuery(id+"F20.opExtrude","SWEPT_FACE",FACE,{"disambiguationData":[OSD([sQuery(id+"F19.wireOp",EDGE,"E50.6.0.0")])]})])],"derivedFrom":makeQuery(id+"F5.opExtrude","CAP_FACE",FACE,{"disambiguationData":[OSD([sQuery(id+"F4.wireOp",EDGE,"E8.top"),sQuery(id+"F4.wireOp",EDGE,"E8.right"),sQuery(id+"F4.wireOp",EDGE,"E8.bottom"),sQuery(id+"F4.wireOp",EDGE,"E9"),sQuery(id+"F4.wireOp",EDGE,"E11.MirrorCS"),sQuery(id+"F4.wireOp",EDGE,"E10.MirrorCS"),sQuery(id+"F4.wireOp",EDGE,"E12.MirrorCS"),sQuery(id+"F4.wireOp",EDGE,"E13.MirrorCS")])],"isStart":true})});
            var Q12;
            Q12=makeQuery(id+"F20.boolean.opBoolean","SPLIT",FACE,{"disambiguationData":[TD([makeQuery(id+"F20.opExtrude","SWEPT_FACE",FACE,{"disambiguationData":[OSD([sQuery(id+"F19.wireOp",EDGE,"E50.7.0.0")])]})])],"derivedFrom":makeQuery(id+"F5.opExtrude","CAP_FACE",FACE,{"disambiguationData":[OSD([sQuery(id+"F4.wireOp",EDGE,"E8.top"),sQuery(id+"F4.wireOp",EDGE,"E8.right"),sQuery(id+"F4.wireOp",EDGE,"E8.bottom"),sQuery(id+"F4.wireOp",EDGE,"E9"),sQuery(id+"F4.wireOp",EDGE,"E11.MirrorCS"),sQuery(id+"F4.wireOp",EDGE,"E10.MirrorCS"),sQuery(id+"F4.wireOp",EDGE,"E12.MirrorCS"),sQuery(id+"F4.wireOp",EDGE,"E13.MirrorCS")])],"isStart":true})});
            var Q13;
            Q13=makeQuery(id+"F20.boolean.opBoolean","SPLIT",FACE,{"disambiguationData":[TD([makeQuery(id+"F20.opExtrude","SWEPT_FACE",FACE,{"disambiguationData":[OSD([sQuery(id+"F19.wireOp",EDGE,"E48.7.0.0")])]})])],"derivedFrom":makeQuery(id+"F5.opExtrude","CAP_FACE",FACE,{"disambiguationData":[OSD([sQuery(id+"F4.wireOp",EDGE,"E8.top"),sQuery(id+"F4.wireOp",EDGE,"E8.right"),sQuery(id+"F4.wireOp",EDGE,"E8.bottom"),sQuery(id+"F4.wireOp",EDGE,"E9"),sQuery(id+"F4.wireOp",EDGE,"E11.MirrorCS"),sQuery(id+"F4.wireOp",EDGE,"E10.MirrorCS"),sQuery(id+"F4.wireOp",EDGE,"E12.MirrorCS"),sQuery(id+"F4.wireOp",EDGE,"E13.MirrorCS")])],"isStart":true})});
            var Q14;
            Q14=makeQuery(id+"F20.boolean.opBoolean","SPLIT",FACE,{"disambiguationData":[TD([makeQuery(id+"F20.opExtrude","SWEPT_FACE",FACE,{"disambiguationData":[OSD([sQuery(id+"F19.wireOp",EDGE,"E48.6.0.0")])]})])],"derivedFrom":makeQuery(id+"F5.opExtrude","CAP_FACE",FACE,{"disambiguationData":[OSD([sQuery(id+"F4.wireOp",EDGE,"E8.top"),sQuery(id+"F4.wireOp",EDGE,"E8.right"),sQuery(id+"F4.wireOp",EDGE,"E8.bottom"),sQuery(id+"F4.wireOp",EDGE,"E9"),sQuery(id+"F4.wireOp",EDGE,"E11.MirrorCS"),sQuery(id+"F4.wireOp",EDGE,"E10.MirrorCS"),sQuery(id+"F4.wireOp",EDGE,"E12.MirrorCS"),sQuery(id+"F4.wireOp",EDGE,"E13.MirrorCS")])],"isStart":true})});
            var Q15;
            Q15=makeQuery(id+"F20.boolean.opBoolean","SPLIT",FACE,{"disambiguationData":[TD([makeQuery(id+"F20.opExtrude","SWEPT_FACE",FACE,{"disambiguationData":[OSD([sQuery(id+"F19.wireOp",EDGE,"E48.5.0.0")])]})])],"derivedFrom":makeQuery(id+"F5.opExtrude","CAP_FACE",FACE,{"disambiguationData":[OSD([sQuery(id+"F4.wireOp",EDGE,"E8.top"),sQuery(id+"F4.wireOp",EDGE,"E8.right"),sQuery(id+"F4.wireOp",EDGE,"E8.bottom"),sQuery(id+"F4.wireOp",EDGE,"E9"),sQuery(id+"F4.wireOp",EDGE,"E11.MirrorCS"),sQuery(id+"F4.wireOp",EDGE,"E10.MirrorCS"),sQuery(id+"F4.wireOp",EDGE,"E12.MirrorCS"),sQuery(id+"F4.wireOp",EDGE,"E13.MirrorCS")])],"isStart":true})});
            var Q16;
            Q16=makeQuery(id+"F20.boolean.opBoolean","SPLIT",FACE,{"disambiguationData":[TD([makeQuery(id+"F20.opExtrude","SWEPT_FACE",FACE,{"disambiguationData":[OSD([sQuery(id+"F19.wireOp",EDGE,"E48.4.0.0")])]})])],"derivedFrom":makeQuery(id+"F5.opExtrude","CAP_FACE",FACE,{"disambiguationData":[OSD([sQuery(id+"F4.wireOp",EDGE,"E8.top"),sQuery(id+"F4.wireOp",EDGE,"E8.right"),sQuery(id+"F4.wireOp",EDGE,"E8.bottom"),sQuery(id+"F4.wireOp",EDGE,"E9"),sQuery(id+"F4.wireOp",EDGE,"E11.MirrorCS"),sQuery(id+"F4.wireOp",EDGE,"E10.MirrorCS"),sQuery(id+"F4.wireOp",EDGE,"E12.MirrorCS"),sQuery(id+"F4.wireOp",EDGE,"E13.MirrorCS")])],"isStart":true})});
            var Q17;
            Q17=makeQuery(id+"F20.boolean.opBoolean","SPLIT",FACE,{"disambiguationData":[TD([makeQuery(id+"F20.opExtrude","SWEPT_FACE",FACE,{"disambiguationData":[OSD([sQuery(id+"F19.wireOp",EDGE,"E48.3.0.0")])]})])],"derivedFrom":makeQuery(id+"F5.opExtrude","CAP_FACE",FACE,{"disambiguationData":[OSD([sQuery(id+"F4.wireOp",EDGE,"E8.top"),sQuery(id+"F4.wireOp",EDGE,"E8.right"),sQuery(id+"F4.wireOp",EDGE,"E8.bottom"),sQuery(id+"F4.wireOp",EDGE,"E9"),sQuery(id+"F4.wireOp",EDGE,"E11.MirrorCS"),sQuery(id+"F4.wireOp",EDGE,"E10.MirrorCS"),sQuery(id+"F4.wireOp",EDGE,"E12.MirrorCS"),sQuery(id+"F4.wireOp",EDGE,"E13.MirrorCS")])],"isStart":true})});
            var Q18;
            Q18=makeQuery(id+"F20.boolean.opBoolean","SPLIT",FACE,{"disambiguationData":[TD([makeQuery(id+"F20.opExtrude","SWEPT_FACE",FACE,{"disambiguationData":[OSD([sQuery(id+"F19.wireOp",EDGE,"E48.2.0.0")])]})])],"derivedFrom":makeQuery(id+"F5.opExtrude","CAP_FACE",FACE,{"disambiguationData":[OSD([sQuery(id+"F4.wireOp",EDGE,"E8.top"),sQuery(id+"F4.wireOp",EDGE,"E8.right"),sQuery(id+"F4.wireOp",EDGE,"E8.bottom"),sQuery(id+"F4.wireOp",EDGE,"E9"),sQuery(id+"F4.wireOp",EDGE,"E11.MirrorCS"),sQuery(id+"F4.wireOp",EDGE,"E10.MirrorCS"),sQuery(id+"F4.wireOp",EDGE,"E12.MirrorCS"),sQuery(id+"F4.wireOp",EDGE,"E13.MirrorCS")])],"isStart":true})});
            var Q19;
            Q19=makeQuery(id+"F20.boolean.opBoolean","SPLIT",FACE,{"disambiguationData":[TD([makeQuery(id+"F20.opExtrude","SWEPT_FACE",FACE,{"disambiguationData":[OSD([sQuery(id+"F19.wireOp",EDGE,"E48.1.0.0")])]})])],"derivedFrom":makeQuery(id+"F5.opExtrude","CAP_FACE",FACE,{"disambiguationData":[OSD([sQuery(id+"F4.wireOp",EDGE,"E8.top"),sQuery(id+"F4.wireOp",EDGE,"E8.right"),sQuery(id+"F4.wireOp",EDGE,"E8.bottom"),sQuery(id+"F4.wireOp",EDGE,"E9"),sQuery(id+"F4.wireOp",EDGE,"E11.MirrorCS"),sQuery(id+"F4.wireOp",EDGE,"E10.MirrorCS"),sQuery(id+"F4.wireOp",EDGE,"E12.MirrorCS"),sQuery(id+"F4.wireOp",EDGE,"E13.MirrorCS")])],"isStart":true})});
            var Q20;
            Q20=makeQuery(id+"F20.boolean.opBoolean","SPLIT",FACE,{"disambiguationData":[TD([makeQuery(id+"F20.opExtrude","SWEPT_FACE",FACE,{"disambiguationData":[OSD([sQuery(id+"F19.wireOp",EDGE,"E47")])]})])],"derivedFrom":makeQuery(id+"F5.opExtrude","CAP_FACE",FACE,{"disambiguationData":[OSD([sQuery(id+"F4.wireOp",EDGE,"E8.top"),sQuery(id+"F4.wireOp",EDGE,"E8.right"),sQuery(id+"F4.wireOp",EDGE,"E8.bottom"),sQuery(id+"F4.wireOp",EDGE,"E9"),sQuery(id+"F4.wireOp",EDGE,"E11.MirrorCS"),sQuery(id+"F4.wireOp",EDGE,"E10.MirrorCS"),sQuery(id+"F4.wireOp",EDGE,"E12.MirrorCS"),sQuery(id+"F4.wireOp",EDGE,"E13.MirrorCS")])],"isStart":true})});
            var Q21;
            Q21=makeQuery(id+"F20.boolean.opBoolean","SPLIT",FACE,{"disambiguationData":[TD([makeQuery(id+"F20.opExtrude","SWEPT_FACE",FACE,{"disambiguationData":[OSD([sQuery(id+"F19.wireOp",EDGE,"E54")])]})])],"derivedFrom":makeQuery(id+"F5.opExtrude","CAP_FACE",FACE,{"disambiguationData":[OSD([sQuery(id+"F4.wireOp",EDGE,"E8.top"),sQuery(id+"F4.wireOp",EDGE,"E8.right"),sQuery(id+"F4.wireOp",EDGE,"E8.bottom"),sQuery(id+"F4.wireOp",EDGE,"E9"),sQuery(id+"F4.wireOp",EDGE,"E11.MirrorCS"),sQuery(id+"F4.wireOp",EDGE,"E10.MirrorCS"),sQuery(id+"F4.wireOp",EDGE,"E12.MirrorCS"),sQuery(id+"F4.wireOp",EDGE,"E13.MirrorCS")])],"isStart":true})});
            var Q22;
            Q22=makeQuery(id+"F20.boolean.opBoolean","SPLIT",FACE,{"disambiguationData":[TD([makeQuery(id+"F20.opExtrude","SWEPT_FACE",FACE,{"disambiguationData":[OSD([sQuery(id+"F19.wireOp",EDGE,"E52")])]})])],"derivedFrom":makeQuery(id+"F5.opExtrude","CAP_FACE",FACE,{"disambiguationData":[OSD([sQuery(id+"F4.wireOp",EDGE,"E8.top"),sQuery(id+"F4.wireOp",EDGE,"E8.right"),sQuery(id+"F4.wireOp",EDGE,"E8.bottom"),sQuery(id+"F4.wireOp",EDGE,"E9"),sQuery(id+"F4.wireOp",EDGE,"E11.MirrorCS"),sQuery(id+"F4.wireOp",EDGE,"E10.MirrorCS"),sQuery(id+"F4.wireOp",EDGE,"E12.MirrorCS"),sQuery(id+"F4.wireOp",EDGE,"E13.MirrorCS")])],"isStart":true})});
            var Q23;
            Q23=makeQuery(id+"F20.boolean.opBoolean","SPLIT",FACE,{"disambiguationData":[TD([makeQuery(id+"F20.opExtrude","SWEPT_FACE",FACE,{"disambiguationData":[OSD([sQuery(id+"F19.wireOp",EDGE,"E55.1.0.0")])]})])],"derivedFrom":makeQuery(id+"F5.opExtrude","CAP_FACE",FACE,{"disambiguationData":[OSD([sQuery(id+"F4.wireOp",EDGE,"E8.top"),sQuery(id+"F4.wireOp",EDGE,"E8.right"),sQuery(id+"F4.wireOp",EDGE,"E8.bottom"),sQuery(id+"F4.wireOp",EDGE,"E9"),sQuery(id+"F4.wireOp",EDGE,"E11.MirrorCS"),sQuery(id+"F4.wireOp",EDGE,"E10.MirrorCS"),sQuery(id+"F4.wireOp",EDGE,"E12.MirrorCS"),sQuery(id+"F4.wireOp",EDGE,"E13.MirrorCS")])],"isStart":true})});
            var Q24;
            Q24=makeQuery(id+"F20.boolean.opBoolean","SPLIT",FACE,{"disambiguationData":[TD([makeQuery(id+"F20.opExtrude","SWEPT_FACE",FACE,{"disambiguationData":[OSD([sQuery(id+"F19.wireOp",EDGE,"E53.1.0.0")])]})])],"derivedFrom":makeQuery(id+"F5.opExtrude","CAP_FACE",FACE,{"disambiguationData":[OSD([sQuery(id+"F4.wireOp",EDGE,"E8.top"),sQuery(id+"F4.wireOp",EDGE,"E8.right"),sQuery(id+"F4.wireOp",EDGE,"E8.bottom"),sQuery(id+"F4.wireOp",EDGE,"E9"),sQuery(id+"F4.wireOp",EDGE,"E11.MirrorCS"),sQuery(id+"F4.wireOp",EDGE,"E10.MirrorCS"),sQuery(id+"F4.wireOp",EDGE,"E12.MirrorCS"),sQuery(id+"F4.wireOp",EDGE,"E13.MirrorCS")])],"isStart":true})});
            var Q25;
            Q25=makeQuery(id+"F20.boolean.opBoolean","SPLIT",FACE,{"disambiguationData":[TD([makeQuery(id+"F20.opExtrude","SWEPT_FACE",FACE,{"disambiguationData":[OSD([sQuery(id+"F19.wireOp",EDGE,"E55.2.0.0")])]})])],"derivedFrom":makeQuery(id+"F5.opExtrude","CAP_FACE",FACE,{"disambiguationData":[OSD([sQuery(id+"F4.wireOp",EDGE,"E8.top"),sQuery(id+"F4.wireOp",EDGE,"E8.right"),sQuery(id+"F4.wireOp",EDGE,"E8.bottom"),sQuery(id+"F4.wireOp",EDGE,"E9"),sQuery(id+"F4.wireOp",EDGE,"E11.MirrorCS"),sQuery(id+"F4.wireOp",EDGE,"E10.MirrorCS"),sQuery(id+"F4.wireOp",EDGE,"E12.MirrorCS"),sQuery(id+"F4.wireOp",EDGE,"E13.MirrorCS")])],"isStart":true})});
            var Q26;
            Q26=makeQuery(id+"F20.boolean.opBoolean","SPLIT",FACE,{"disambiguationData":[TD([makeQuery(id+"F20.opExtrude","SWEPT_FACE",FACE,{"disambiguationData":[OSD([sQuery(id+"F19.wireOp",EDGE,"E53.2.0.0")])]})])],"derivedFrom":makeQuery(id+"F5.opExtrude","CAP_FACE",FACE,{"disambiguationData":[OSD([sQuery(id+"F4.wireOp",EDGE,"E8.top"),sQuery(id+"F4.wireOp",EDGE,"E8.right"),sQuery(id+"F4.wireOp",EDGE,"E8.bottom"),sQuery(id+"F4.wireOp",EDGE,"E9"),sQuery(id+"F4.wireOp",EDGE,"E11.MirrorCS"),sQuery(id+"F4.wireOp",EDGE,"E10.MirrorCS"),sQuery(id+"F4.wireOp",EDGE,"E12.MirrorCS"),sQuery(id+"F4.wireOp",EDGE,"E13.MirrorCS")])],"isStart":true})});
            var Q27;
            Q27=makeQuery(id+"F20.boolean.opBoolean","SPLIT",FACE,{"disambiguationData":[TD([makeQuery(id+"F20.opExtrude","SWEPT_FACE",FACE,{"disambiguationData":[OSD([sQuery(id+"F19.wireOp",EDGE,"E55.3.0.0")])]})])],"derivedFrom":makeQuery(id+"F5.opExtrude","CAP_FACE",FACE,{"disambiguationData":[OSD([sQuery(id+"F4.wireOp",EDGE,"E8.top"),sQuery(id+"F4.wireOp",EDGE,"E8.right"),sQuery(id+"F4.wireOp",EDGE,"E8.bottom"),sQuery(id+"F4.wireOp",EDGE,"E9"),sQuery(id+"F4.wireOp",EDGE,"E11.MirrorCS"),sQuery(id+"F4.wireOp",EDGE,"E10.MirrorCS"),sQuery(id+"F4.wireOp",EDGE,"E12.MirrorCS"),sQuery(id+"F4.wireOp",EDGE,"E13.MirrorCS")])],"isStart":true})});
            var Q28;
            Q28=makeQuery(id+"F20.boolean.opBoolean","SPLIT",FACE,{"disambiguationData":[TD([makeQuery(id+"F20.opExtrude","SWEPT_FACE",FACE,{"disambiguationData":[OSD([sQuery(id+"F19.wireOp",EDGE,"E53.3.0.0")])]})])],"derivedFrom":makeQuery(id+"F5.opExtrude","CAP_FACE",FACE,{"disambiguationData":[OSD([sQuery(id+"F4.wireOp",EDGE,"E8.top"),sQuery(id+"F4.wireOp",EDGE,"E8.right"),sQuery(id+"F4.wireOp",EDGE,"E8.bottom"),sQuery(id+"F4.wireOp",EDGE,"E9"),sQuery(id+"F4.wireOp",EDGE,"E11.MirrorCS"),sQuery(id+"F4.wireOp",EDGE,"E10.MirrorCS"),sQuery(id+"F4.wireOp",EDGE,"E12.MirrorCS"),sQuery(id+"F4.wireOp",EDGE,"E13.MirrorCS")])],"isStart":true})});
            var Q29;
            Q29=makeQuery(id+"F20.boolean.opBoolean","SPLIT",FACE,{"disambiguationData":[TD([makeQuery(id+"F20.opExtrude","SWEPT_FACE",FACE,{"disambiguationData":[OSD([sQuery(id+"F19.wireOp",EDGE,"E55.4.0.0")])]})])],"derivedFrom":makeQuery(id+"F5.opExtrude","CAP_FACE",FACE,{"disambiguationData":[OSD([sQuery(id+"F4.wireOp",EDGE,"E8.top"),sQuery(id+"F4.wireOp",EDGE,"E8.right"),sQuery(id+"F4.wireOp",EDGE,"E8.bottom"),sQuery(id+"F4.wireOp",EDGE,"E9"),sQuery(id+"F4.wireOp",EDGE,"E11.MirrorCS"),sQuery(id+"F4.wireOp",EDGE,"E10.MirrorCS"),sQuery(id+"F4.wireOp",EDGE,"E12.MirrorCS"),sQuery(id+"F4.wireOp",EDGE,"E13.MirrorCS")])],"isStart":true})});
            var Q30;
            Q30=makeQuery(id+"F20.boolean.opBoolean","SPLIT",FACE,{"disambiguationData":[TD([makeQuery(id+"F20.opExtrude","SWEPT_FACE",FACE,{"disambiguationData":[OSD([sQuery(id+"F19.wireOp",EDGE,"E53.4.0.0")])]})])],"derivedFrom":makeQuery(id+"F5.opExtrude","CAP_FACE",FACE,{"disambiguationData":[OSD([sQuery(id+"F4.wireOp",EDGE,"E8.top"),sQuery(id+"F4.wireOp",EDGE,"E8.right"),sQuery(id+"F4.wireOp",EDGE,"E8.bottom"),sQuery(id+"F4.wireOp",EDGE,"E9"),sQuery(id+"F4.wireOp",EDGE,"E11.MirrorCS"),sQuery(id+"F4.wireOp",EDGE,"E10.MirrorCS"),sQuery(id+"F4.wireOp",EDGE,"E12.MirrorCS"),sQuery(id+"F4.wireOp",EDGE,"E13.MirrorCS")])],"isStart":true})});
            var Q31;
            Q31=makeQuery(id+"F20.boolean.opBoolean","SPLIT",FACE,{"disambiguationData":[TD([makeQuery(id+"F20.opExtrude","SWEPT_FACE",FACE,{"disambiguationData":[OSD([sQuery(id+"F19.wireOp",EDGE,"E53.5.0.0")])]})])],"derivedFrom":makeQuery(id+"F5.opExtrude","CAP_FACE",FACE,{"disambiguationData":[OSD([sQuery(id+"F4.wireOp",EDGE,"E8.top"),sQuery(id+"F4.wireOp",EDGE,"E8.right"),sQuery(id+"F4.wireOp",EDGE,"E8.bottom"),sQuery(id+"F4.wireOp",EDGE,"E9"),sQuery(id+"F4.wireOp",EDGE,"E11.MirrorCS"),sQuery(id+"F4.wireOp",EDGE,"E10.MirrorCS"),sQuery(id+"F4.wireOp",EDGE,"E12.MirrorCS"),sQuery(id+"F4.wireOp",EDGE,"E13.MirrorCS")])],"isStart":true})});
            var Q32;
            Q32=makeQuery(id+"F20.boolean.opBoolean","SPLIT",FACE,{"disambiguationData":[TD([makeQuery(id+"F20.opExtrude","SWEPT_FACE",FACE,{"disambiguationData":[OSD([sQuery(id+"F19.wireOp",EDGE,"E55.5.0.0")])]})])],"derivedFrom":makeQuery(id+"F5.opExtrude","CAP_FACE",FACE,{"disambiguationData":[OSD([sQuery(id+"F4.wireOp",EDGE,"E8.top"),sQuery(id+"F4.wireOp",EDGE,"E8.right"),sQuery(id+"F4.wireOp",EDGE,"E8.bottom"),sQuery(id+"F4.wireOp",EDGE,"E9"),sQuery(id+"F4.wireOp",EDGE,"E11.MirrorCS"),sQuery(id+"F4.wireOp",EDGE,"E10.MirrorCS"),sQuery(id+"F4.wireOp",EDGE,"E12.MirrorCS"),sQuery(id+"F4.wireOp",EDGE,"E13.MirrorCS")])],"isStart":true})});
            var Q33;
            Q33=makeQuery(id+"F20.boolean.opBoolean","SPLIT",FACE,{"disambiguationData":[TD([makeQuery(id+"F20.opExtrude","SWEPT_FACE",FACE,{"disambiguationData":[OSD([sQuery(id+"F19.wireOp",EDGE,"E55.6.0.0")])]})])],"derivedFrom":makeQuery(id+"F5.opExtrude","CAP_FACE",FACE,{"disambiguationData":[OSD([sQuery(id+"F4.wireOp",EDGE,"E8.top"),sQuery(id+"F4.wireOp",EDGE,"E8.right"),sQuery(id+"F4.wireOp",EDGE,"E8.bottom"),sQuery(id+"F4.wireOp",EDGE,"E9"),sQuery(id+"F4.wireOp",EDGE,"E11.MirrorCS"),sQuery(id+"F4.wireOp",EDGE,"E10.MirrorCS"),sQuery(id+"F4.wireOp",EDGE,"E12.MirrorCS"),sQuery(id+"F4.wireOp",EDGE,"E13.MirrorCS")])],"isStart":true})});
            var Q34;
            Q34=makeQuery(id+"F20.boolean.opBoolean","SPLIT",FACE,{"disambiguationData":[TD([makeQuery(id+"F20.opExtrude","SWEPT_FACE",FACE,{"disambiguationData":[OSD([sQuery(id+"F19.wireOp",EDGE,"E53.6.0.0")])]})])],"derivedFrom":makeQuery(id+"F5.opExtrude","CAP_FACE",FACE,{"disambiguationData":[OSD([sQuery(id+"F4.wireOp",EDGE,"E8.top"),sQuery(id+"F4.wireOp",EDGE,"E8.right"),sQuery(id+"F4.wireOp",EDGE,"E8.bottom"),sQuery(id+"F4.wireOp",EDGE,"E9"),sQuery(id+"F4.wireOp",EDGE,"E11.MirrorCS"),sQuery(id+"F4.wireOp",EDGE,"E10.MirrorCS"),sQuery(id+"F4.wireOp",EDGE,"E12.MirrorCS"),sQuery(id+"F4.wireOp",EDGE,"E13.MirrorCS")])],"isStart":true})});
            var Q35;
            Q35=makeQuery(id+"F20.boolean.opBoolean","SPLIT",FACE,{"disambiguationData":[TD([makeQuery(id+"F20.opExtrude","SWEPT_FACE",FACE,{"disambiguationData":[OSD([sQuery(id+"F19.wireOp",EDGE,"E53.7.0.0")])]})])],"derivedFrom":makeQuery(id+"F5.opExtrude","CAP_FACE",FACE,{"disambiguationData":[OSD([sQuery(id+"F4.wireOp",EDGE,"E8.top"),sQuery(id+"F4.wireOp",EDGE,"E8.right"),sQuery(id+"F4.wireOp",EDGE,"E8.bottom"),sQuery(id+"F4.wireOp",EDGE,"E9"),sQuery(id+"F4.wireOp",EDGE,"E11.MirrorCS"),sQuery(id+"F4.wireOp",EDGE,"E10.MirrorCS"),sQuery(id+"F4.wireOp",EDGE,"E12.MirrorCS"),sQuery(id+"F4.wireOp",EDGE,"E13.MirrorCS")])],"isStart":true})});
            var Q36;
            Q36=makeQuery(id+"F20.boolean.opBoolean","SPLIT",FACE,{"disambiguationData":[TD([makeQuery(id+"F20.opExtrude","SWEPT_FACE",FACE,{"disambiguationData":[OSD([sQuery(id+"F19.wireOp",EDGE,"E55.7.0.0")])]})])],"derivedFrom":makeQuery(id+"F5.opExtrude","CAP_FACE",FACE,{"disambiguationData":[OSD([sQuery(id+"F4.wireOp",EDGE,"E8.top"),sQuery(id+"F4.wireOp",EDGE,"E8.right"),sQuery(id+"F4.wireOp",EDGE,"E8.bottom"),sQuery(id+"F4.wireOp",EDGE,"E9"),sQuery(id+"F4.wireOp",EDGE,"E11.MirrorCS"),sQuery(id+"F4.wireOp",EDGE,"E10.MirrorCS"),sQuery(id+"F4.wireOp",EDGE,"E12.MirrorCS"),sQuery(id+"F4.wireOp",EDGE,"E13.MirrorCS")])],"isStart":true})});
            extrude(context, id + "F21", {"entities" : qUnion([Q0, Q1, Q2, Q3, Q4, Q5, Q6, Q7, Q8, Q9, Q10, Q11, Q12, Q13, Q14, Q15, Q16, Q17, Q18, Q19, Q20, Q21, Q22, Q23, Q24, Q25, Q26, Q27, Q28, Q29, Q30, Q31, Q32, Q33, Q34, Q35, Q36]), "operationType" : NewBodyOperationType.ADD, "depth" : 2.5 * mm, "offsetDistance" : 25 * mm});
        }
        {
            var Q0;
            Q0=makeQuery(id+"F1.opExtrude","SWEPT_FACE",FACE,{"disambiguationData":[OSD([sQuery(id+"F0.wireOp",EDGE,"E6")])]});
            var sketch = newSketch(context, id + "F22", { "sketchPlane" : qUnion([Q0])});
            skLineSegment(sketch, "E56.bottom", {"start": v(3.9, 17.7) * mm, "end": v(26.92, 17.7) * mm});
            skLineSegment(sketch, "E56.top", {"start": v(3.9, 0) * mm, "end": v(26.92, 0) * mm});
            skLineSegment(sketch, "E56.left", {"start": v(3.9, 17.7) * mm, "end": v(3.9, 0) * mm});
            skLineSegment(sketch, "E56.right", {"start": v(26.92, 17.7) * mm, "end": v(26.92, 0) * mm});
            skLineSegment(sketch, "E57.bottom", {"start": v(5.38, 16.55) * mm, "end": v(25.44, 16.55) * mm});
            skLineSegment(sketch, "E57.top", {"start": v(5.38, 5.37) * mm, "end": v(25.44, 5.37) * mm});
            skLineSegment(sketch, "E57.left", {"start": v(5.38, 16.55) * mm, "end": v(5.38, 5.37) * mm});
            skLineSegment(sketch, "E57.right", {"start": v(25.44, 16.55) * mm, "end": v(25.44, 5.37) * mm});
            skSolve(sketch);
        }
        {
            var Q0;
            Q0=makeQuery(id+"F22.imprint","IMPRINT",FACE,{"disambiguationData":[TD([[makeQuery(id+"F22.imprint","IMPRINT",EDGE,{"derivedFrom":sQuery(id+"F22.wireOp",EDGE,"E56.bottom")}),-1.0]])]});
            extrude(context, id + "F23", {"entities" : qUnion([Q0]), "operationType" : NewBodyOperationType.ADD, "depth" : 1.5 * mm, "offsetDistance" : 25 * mm});
        }
        {
            var Q0;
            Q0=makeQuery(id+"F23.opExtrude","CAP_FACE",FACE,{"disambiguationData":[OSD([sQuery(id+"F22.wireOp",EDGE,"E56.bottom"),sQuery(id+"F22.wireOp",EDGE,"E56.top"),sQuery(id+"F22.wireOp",EDGE,"E56.left"),sQuery(id+"F22.wireOp",EDGE,"E56.right"),sQuery(id+"F22.wireOp",EDGE,"E57.bottom"),sQuery(id+"F22.wireOp",EDGE,"E57.top"),sQuery(id+"F22.wireOp",EDGE,"E57.left"),sQuery(id+"F22.wireOp",EDGE,"E57.right")])],"isStart":false});
            var sketch = newSketch(context, id + "F24", { "sketchPlane" : qUnion([Q0])});
            skCircle(sketch, "E58", {"center": v(6.07, 3.86) * mm, "radius": 0.75 * mm});
            skCircle(sketch, "E59.1.0.0", {"center": v(8.72, 3.86) * mm, "radius": 0.75 * mm});
            skCircle(sketch, "E59.2.0.0", {"center": v(11.37, 3.86) * mm, "radius": 0.75 * mm});
            skCircle(sketch, "E59.3.0.0", {"center": v(14.02, 3.87) * mm, "radius": 0.75 * mm});
            skCircle(sketch, "E59.4.0.0", {"center": v(16.67, 3.87) * mm, "radius": 0.75 * mm});
            skCircle(sketch, "E59.5.0.0", {"center": v(19.32, 3.87) * mm, "radius": 0.75 * mm});
            skCircle(sketch, "E59.6.0.0", {"center": v(21.97, 3.88) * mm, "radius": 0.75 * mm});
            skCircle(sketch, "E59.7.0.0", {"center": v(24.62, 3.88) * mm, "radius": 0.75 * mm});
            skLineSegment(sketch, "E59.direction1", {"start": v(6.07, 3.86) * mm, "end": v(8.72, 3.86) * mm, "construction": true});
            skCircle(sketch, "E60", {"center": v(6.04, 1.7) * mm, "radius": 0.75 * mm});
            skCircle(sketch, "E61.1.0.0", {"center": v(8.69, 1.7) * mm, "radius": 0.75 * mm});
            skCircle(sketch, "E61.2.0.0", {"center": v(11.34, 1.7) * mm, "radius": 0.75 * mm});
            skCircle(sketch, "E61.3.0.0", {"center": v(13.99, 1.7) * mm, "radius": 0.75 * mm});
            skCircle(sketch, "E61.4.0.0", {"center": v(16.64, 1.71) * mm, "radius": 0.75 * mm});
            skCircle(sketch, "E61.5.0.0", {"center": v(19.29, 1.71) * mm, "radius": 0.75 * mm});
            skCircle(sketch, "E61.6.0.0", {"center": v(22.05, 1.75) * mm, "radius": 0.75 * mm});
            skCircle(sketch, "E61.7.0.0", {"center": v(24.59, 1.72) * mm, "radius": 0.75 * mm});
            skSolve(sketch);
        }
        {
            var Q0;
            Q0 = qSketchRegion(id + "F24", true);
            extrude(context, id + "F25", {"entities" : qUnion([Q0]), "operationType" : NewBodyOperationType.ADD, "depth" : 1 * mm, "offsetDistance" : 25 * mm});
        }
    });
